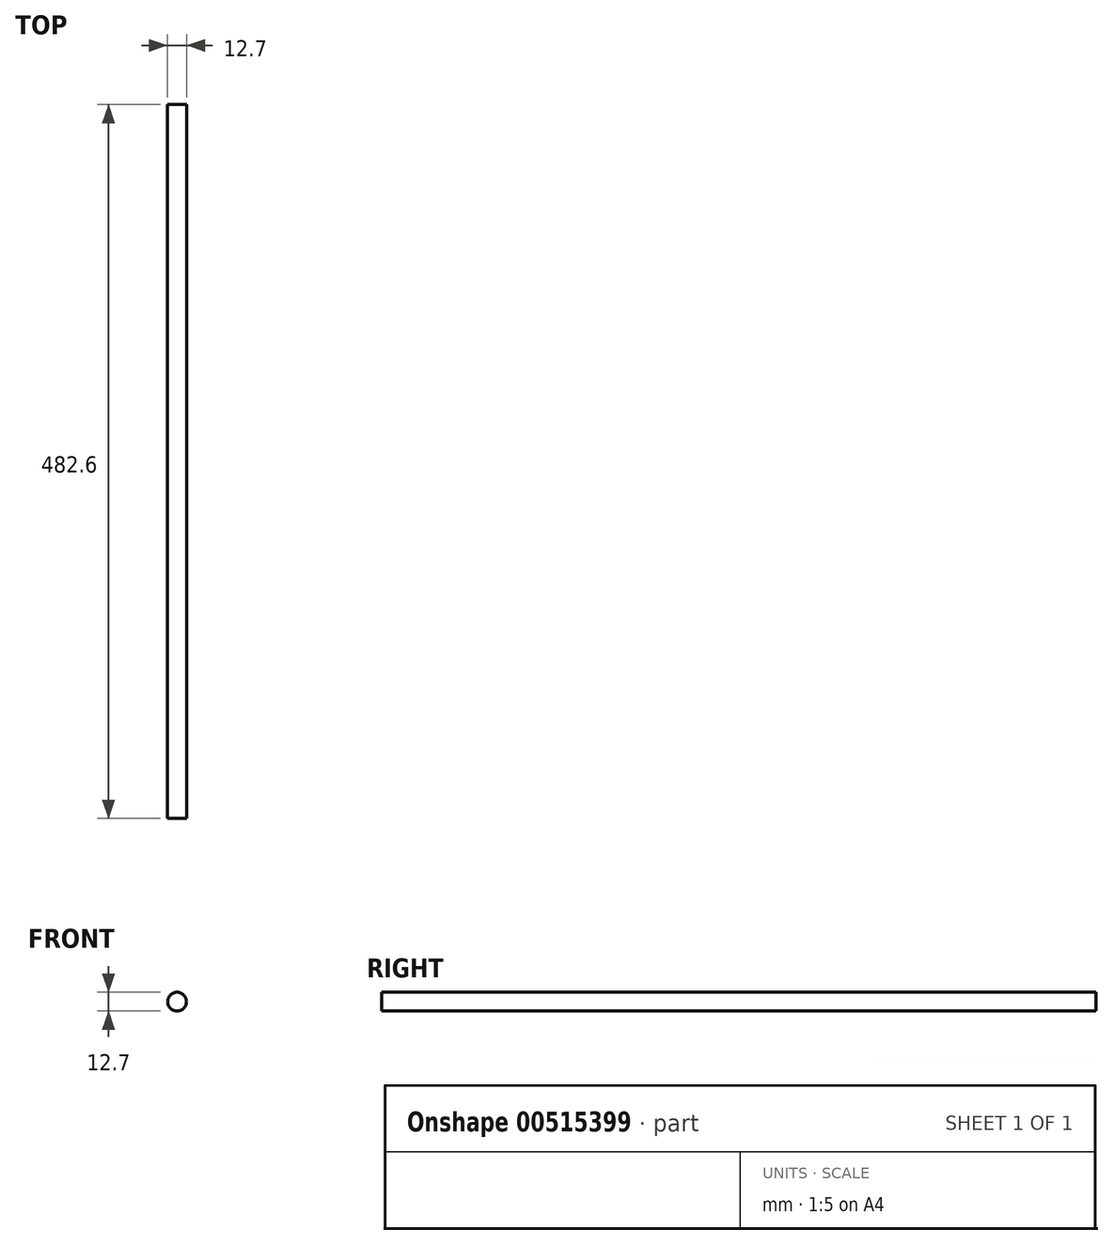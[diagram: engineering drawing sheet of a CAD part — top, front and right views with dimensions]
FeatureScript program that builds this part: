
annotation { "Feature Type Name" : "Feature", "Feature Type Description" : "" }
export const myFeature = defineFeature(function(context is Context, id is Id, definition is map)
    precondition{}
    {
        {
            var Q0;
            Q0=qCreatedBy(makeId("Front.planeOp"),FACE);
            var sketch = newSketch(context, id + "F0", { "sketchPlane" : qUnion([Q0])});
            skCircle(sketch, "E0", {"center": v(0, 0) * mm, "radius": 6.35 * mm});
            skSolve(sketch);
        }
        {
            var Q0;
            Q0=makeQuery(id+"F0.imprint","IMPRINT",FACE,{"disambiguationData":[TD([[makeQuery(id+"F0.imprint","IMPRINT",EDGE,{"derivedFrom":sQuery(id+"F0.wireOp",EDGE,"E0")}),1.0]])]});
            extrude(context, id + "F1", {"entities" : qUnion([Q0]), "depth" : 482.6 * mm, "offsetDistance" : 25.4 * mm});
        }
    });
